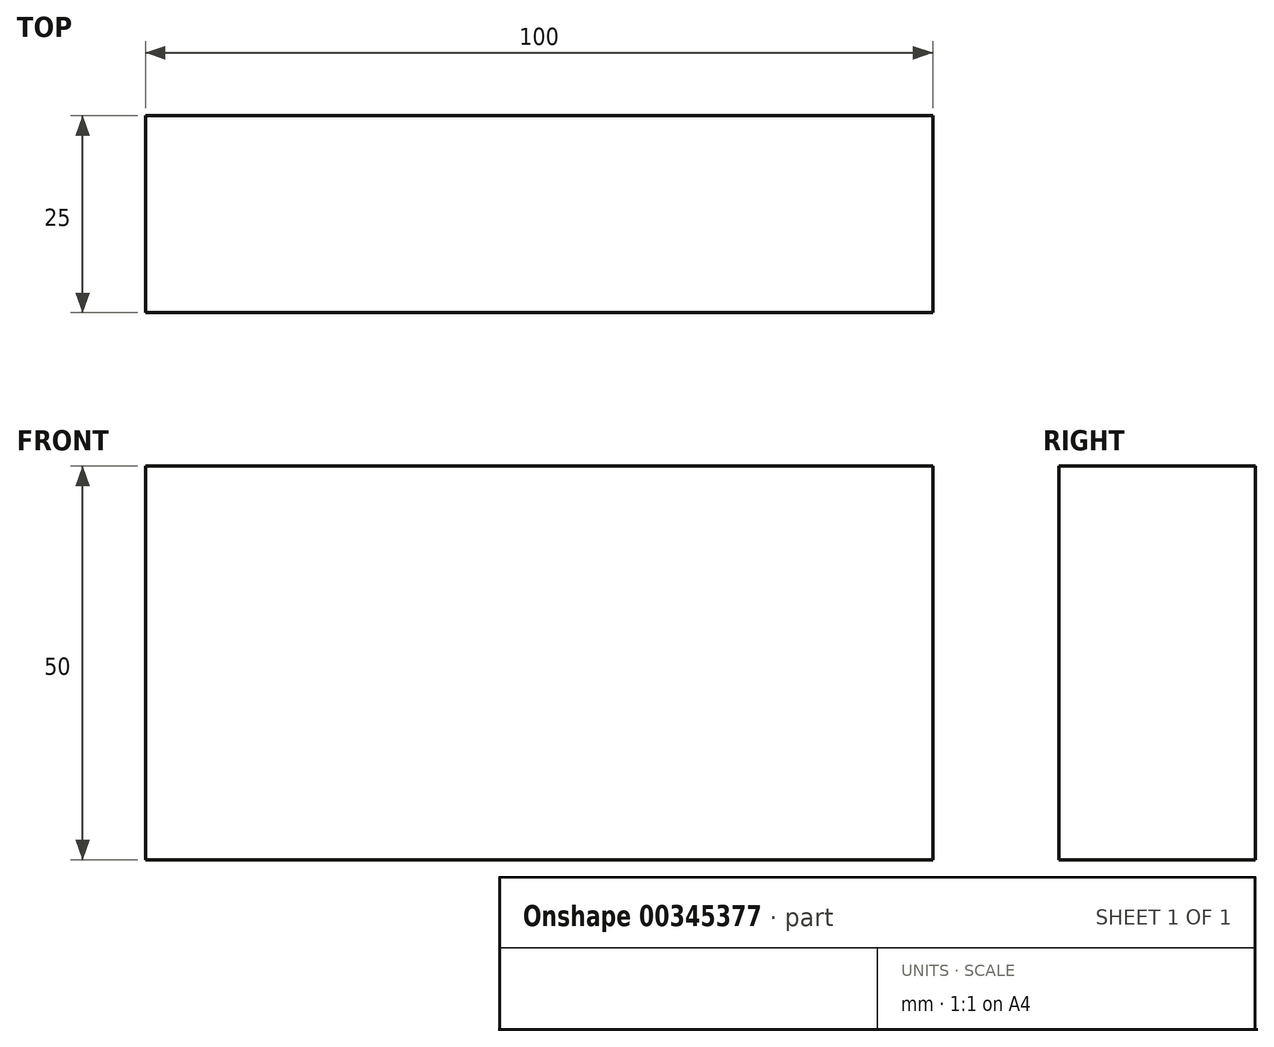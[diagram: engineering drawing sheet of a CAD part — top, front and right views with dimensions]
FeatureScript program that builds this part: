
annotation { "Feature Type Name" : "Feature", "Feature Type Description" : "" }
export const myFeature = defineFeature(function(context is Context, id is Id, definition is map)
    precondition{}
    {
        {
            var Q0;
            Q0=qCreatedBy(makeId("Front.planeOp"),FACE);
            var sketch = newSketch(context, id + "F0", { "sketchPlane" : qUnion([Q0])});
            skLineSegment(sketch, "E0.bottom", {"start": v(-48.54, 22.47) * mm, "end": v(51.46, 22.47) * mm});
            skLineSegment(sketch, "E0.top", {"start": v(-48.54, -27.53) * mm, "end": v(51.46, -27.53) * mm});
            skLineSegment(sketch, "E0.left", {"start": v(-48.54, 22.47) * mm, "end": v(-48.54, -27.53) * mm});
            skLineSegment(sketch, "E0.right", {"start": v(51.46, 22.47) * mm, "end": v(51.46, -27.53) * mm});
            skSolve(sketch);
        }
        {
            var Q0;
            Q0 = qSketchRegion(id + "F0", true);
            extrude(context, id + "F1", {"entities" : qUnion([Q0]), "depth" : 25 * mm});
        }
    });
